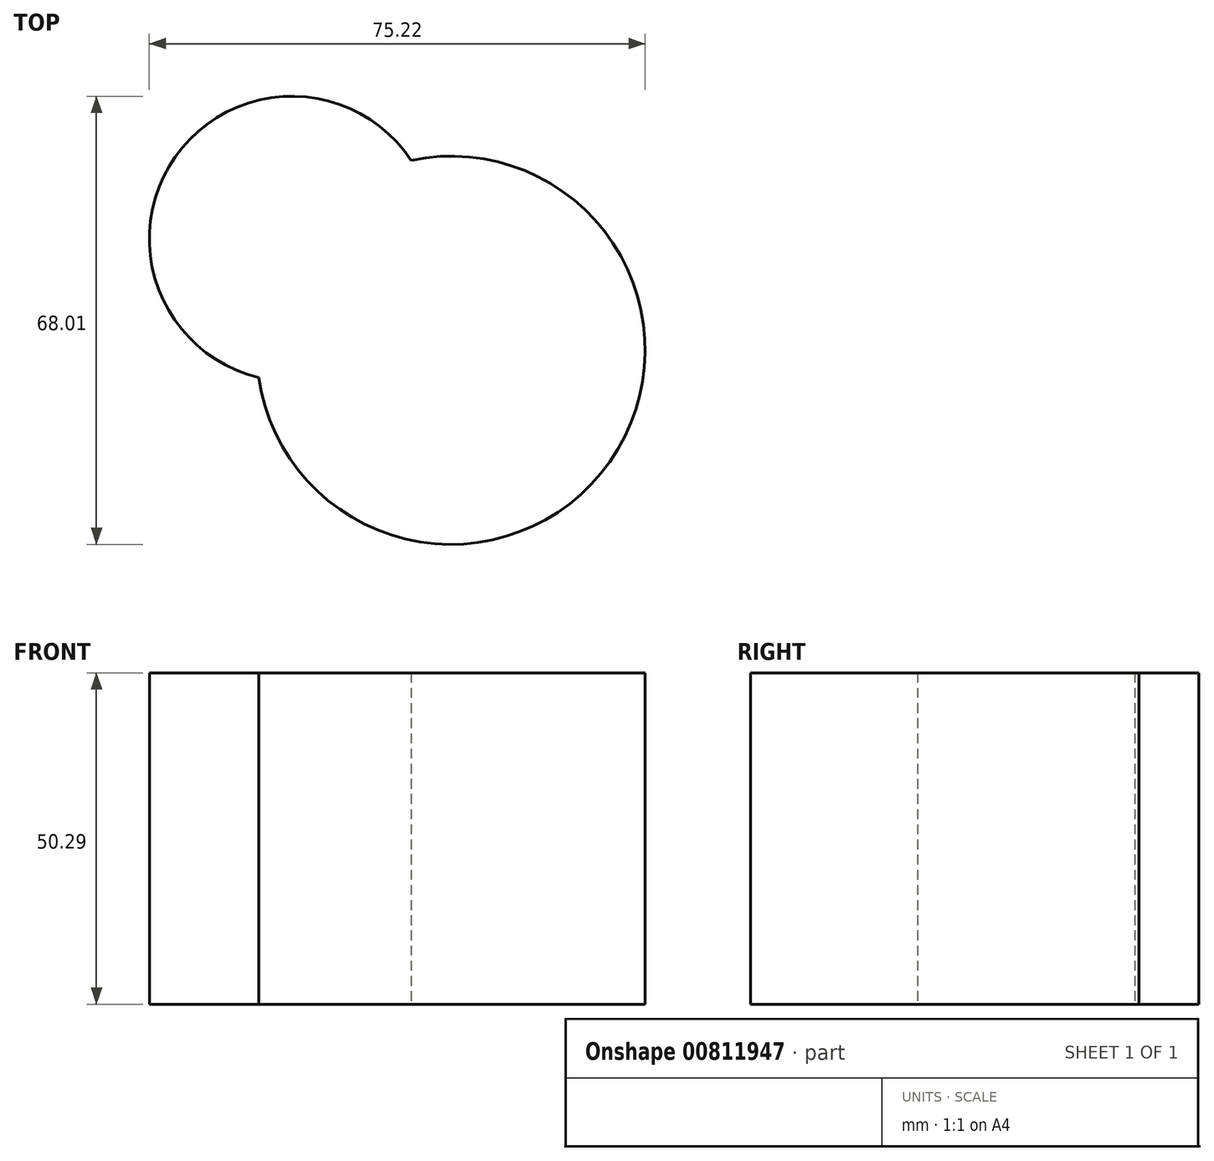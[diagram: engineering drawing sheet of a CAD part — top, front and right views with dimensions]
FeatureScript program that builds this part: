
annotation { "Feature Type Name" : "Feature", "Feature Type Description" : "" }
export const myFeature = defineFeature(function(context is Context, id is Id, definition is map)
    precondition{}
    {
        {
            var Q0;
            Q0=qCreatedBy(makeId("Top.planeOp"),FACE);
            var sketch = newSketch(context, id + "F0", { "sketchPlane" : qUnion([Q0])});
            skCircle(sketch, "E0", {"center": v(0, -1.39) * mm, "radius": 29.46 * mm});
            skCircle(sketch, "E1", {"center": v(-24.12, 15.53) * mm, "radius": 21.64 * mm});
            skSolve(sketch);
        }
        {
            var Q0;
            Q0 = qSketchRegion(id + "F0", true);
            extrude(context, id + "F1", {"entities" : qUnion([Q0]), "depth" : 50.3 * mm, "offsetDistance" : 25.4 * mm});
        }
    });
